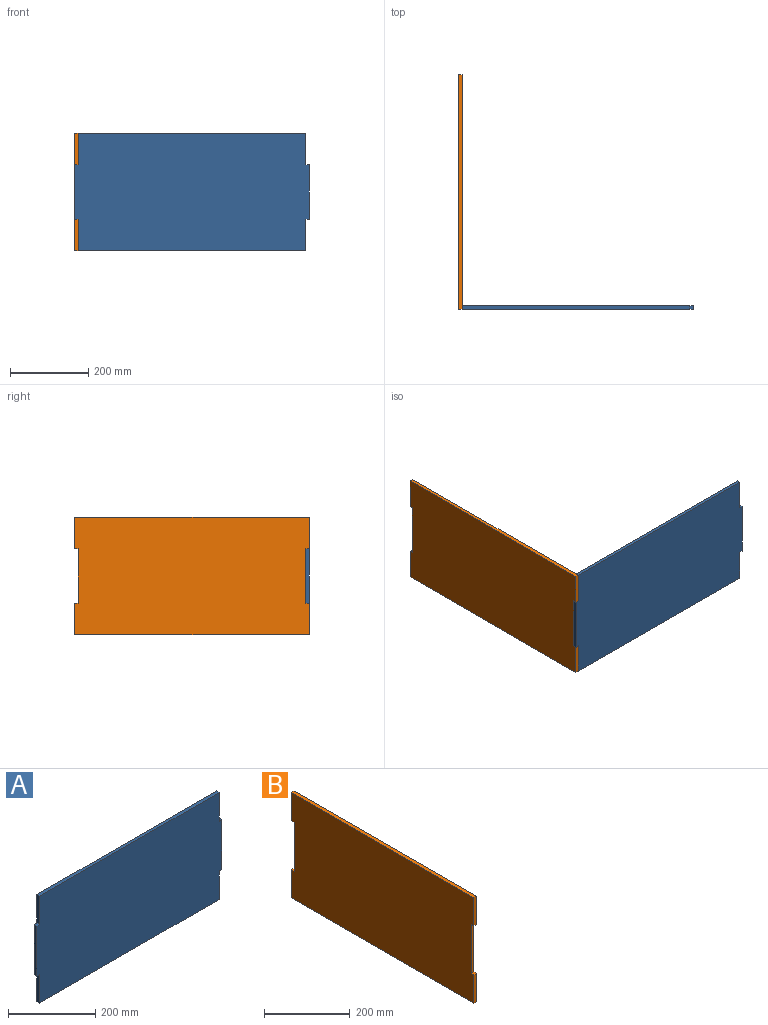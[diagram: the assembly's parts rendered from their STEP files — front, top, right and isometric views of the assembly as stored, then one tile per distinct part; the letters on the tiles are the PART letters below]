
ASSEMBLY  parts=2 mates=1
PART A: 14 faces, bbox 600x9x300 mm
  f0: plane 582x9mm, normal (0,0,1), area 5238mm2, adj f1,f11,f12,f13
  f1: plane 80x9mm, normal (-1,0,0), area 720mm2, adj f0,f2,f12,f13
  f2: plane 9x9mm, normal (0,0,1), area 81mm2, adj f1,f3,f12,f13
  f3: plane 140x9mm, normal (-1,0,0), area 1260mm2, adj f2,f4,f12,f13
  f4: plane 9x9mm, normal (0,0,-1), area 81mm2, adj f3,f5,f12,f13
  f5: plane 80x9mm, normal (-1,0,0), area 720mm2, adj f4,f6,f12,f13
  f6: plane 582x9mm, normal (0,0,-1), area 5238mm2, adj f5,f7,f12,f13
  f7: plane 80x9mm, normal (1,0,0), area 720mm2, adj f6,f8,f12,f13
  f8: plane 9x9mm, normal (0,0,-1), area 81mm2, adj f7,f9,f12,f13
  f9: plane 140x9mm, normal (1,0,0), area 1260mm2, adj f8,f10,f12,f13
  f10: plane 9x9mm, normal (0,0,1), area 81mm2, adj f9,f11,f12,f13
  f11: plane 80x9mm, normal (1,0,0), area 720mm2, adj f0,f10,f12,f13
  f12: plane 600x300mm, normal (0,-1,0), area 177120mm2, adj f0,f1,f2,f3,f4,f5,f6,f7
  f13: plane 600x300mm, normal (0,1,0), area 177120mm2, adj f0,f1,f2,f3,f4,f5,f6,f7
PART B: 14 faces, bbox 9x600x300 mm
  f0: plane 80x9mm, normal (0,1,0), area 720mm2, adj f1,f11,f12,f13
  f1: plane 9x9mm, normal (0,0,1), area 81mm2, adj f0,f2,f12,f13
  f2: plane 140x9mm, normal (0,1,0), area 1260mm2, adj f1,f3,f12,f13
  f3: plane 9x9mm, normal (0,0,-1), area 81mm2, adj f2,f4,f12,f13
  f4: plane 80x9mm, normal (0,1,0), area 720mm2, adj f3,f5,f12,f13
  f5: plane 600x9mm, normal (0,0,1), area 5400mm2, adj f4,f6,f12,f13
  f6: plane 80x9mm, normal (0,-1,0), area 720mm2, adj f5,f7,f12,f13
  f7: plane 9x9mm, normal (0,0,-1), area 81mm2, adj f6,f8,f12,f13
  f8: plane 140x9mm, normal (0,-1,0), area 1260mm2, adj f7,f9,f12,f13
  f9: plane 9x9mm, normal (0,0,1), area 81mm2, adj f8,f10,f12,f13
  f10: plane 80x9mm, normal (0,-1,0), area 720mm2, adj f9,f11,f12,f13
  f11: plane 600x9mm, normal (0,0,-1), area 5400mm2, adj f0,f10,f12,f13
  f12: plane 600x300mm, normal (1,0,0), area 177480mm2, adj f0,f1,f2,f3,f4,f5,f6,f7
  f13: plane 600x300mm, normal (-1,0,0), area 177480mm2, adj f0,f1,f2,f3,f4,f5,f6,f7
PLACE A t=(-59.83,-52.98,-66.22)mm
PLACE B t=(-371,275.87,-127.41)mm
MATE fastened B.f7 <-> A.f2  axis (0,0,-1) through (-366.5,-57.48,4.79)mm
